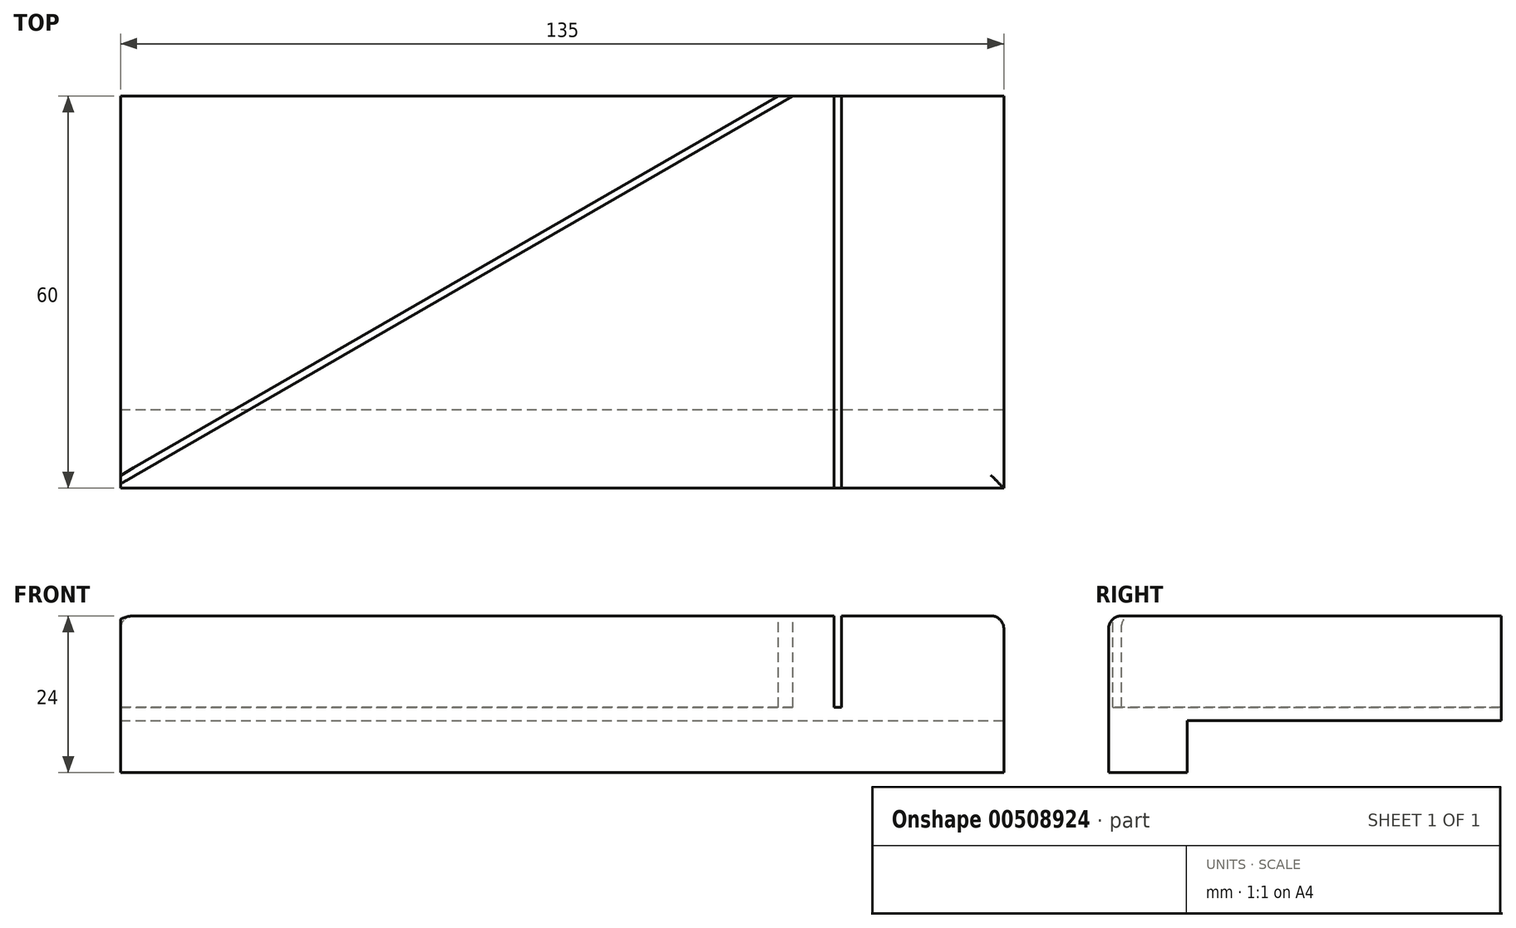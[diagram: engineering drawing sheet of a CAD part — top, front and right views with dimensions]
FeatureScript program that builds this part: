
annotation { "Feature Type Name" : "Feature", "Feature Type Description" : "" }
export const myFeature = defineFeature(function(context is Context, id is Id, definition is map)
    precondition{}
    {
        {
            var Q0;
            Q0=qCreatedBy(makeId("Top.planeOp"),FACE);
            var sketch = newSketch(context, id + "F0", { "sketchPlane" : qUnion([Q0])});
            skLineSegment(sketch, "E0.bottom", {"start": v(67.5, -30) * mm, "end": v(-67.5, -30) * mm});
            skLineSegment(sketch, "E0.top", {"start": v(67.5, 30) * mm, "end": v(-67.5, 30) * mm});
            skLineSegment(sketch, "E0.left", {"start": v(67.5, -30) * mm, "end": v(67.5, 30) * mm});
            skLineSegment(sketch, "E0.right", {"start": v(-67.5, -30) * mm, "end": v(-67.5, 30) * mm});
            skPoint(sketch, "E0.middle", {"position": v(0, 0) * mm});
            skSolve(sketch);
        }
        {
            var Q0;
            Q0 = qSketchRegion(id + "F0", true);
            extrude(context, id + "F1", {"entities" : qUnion([Q0]), "depth" : 16 * mm});
        }
        {
            var Q0;
            Q0=makeQuery(id+"F1.opExtrude","CAP_FACE",FACE,{"disambiguationData":[OSD([sQuery(id+"F0.wireOp",EDGE,"E0.bottom"),sQuery(id+"F0.wireOp",EDGE,"E0.top"),sQuery(id+"F0.wireOp",EDGE,"E0.left"),sQuery(id+"F0.wireOp",EDGE,"E0.right")])],"isStart":false});
            var sketch = newSketch(context, id + "F2", { "sketchPlane" : qUnion([Q0])});
            skLineSegment(sketch, "E1", {"start": v(15.2, 30) * mm, "end": v(-67.5, -17.74) * mm});
            skLineSegment(sketch, "E2", {"start": v(33.03, 30) * mm, "end": v(-67.5, -28.04) * mm});
            skLineSegment(sketch, "E3", {"start": v(41.55, 30) * mm, "end": v(41.55, -30) * mm});
            skLineSegment(sketch, "E4", {"start": v(-67.5, -18.78) * mm, "end": v(17, 30) * mm});
            skLineSegment(sketch, "E5", {"start": v(-67.5, -29.33) * mm, "end": v(35.27, 30) * mm});
            skLineSegment(sketch, "E6", {"start": v(15.2, 30) * mm, "end": v(17, 30) * mm});
            skLineSegment(sketch, "E7", {"start": v(33.03, 30) * mm, "end": v(35.27, 30) * mm});
            skLineSegment(sketch, "E8", {"start": v(-67.5, -29.33) * mm, "end": v(-67.5, -28.04) * mm});
            skLineSegment(sketch, "E9", {"start": v(-67.5, -18.78) * mm, "end": v(-67.5, -17.74) * mm});
            skLineSegment(sketch, "E10", {"start": v(41.55, 30) * mm, "end": v(42.67, 30) * mm});
            skLineSegment(sketch, "E11", {"start": v(42.67, 30) * mm, "end": v(42.67, -30) * mm});
            skLineSegment(sketch, "E12", {"start": v(42.67, -30) * mm, "end": v(41.55, -30) * mm});
            skLineSegment(sketch, "E13", {"start": v(-67.5, -29.33) * mm, "end": v(27.72, -29.33) * mm, "construction": true});
            skLineSegment(sketch, "E14", {"start": v(-67.5, -28.04) * mm, "end": v(-66.94, -29) * mm, "construction": true});
            skLineSegment(sketch, "E15", {"start": v(-67.5, -17.74) * mm, "end": v(-67.05, -18.52) * mm, "construction": true});
            skSolve(sketch);
        }
        {
            var Q0;
            Q0=makeQuery(id+"F2.imprint","IMPRINT",FACE,{"disambiguationData":[TD([[makeQuery(id+"F2.imprint","IMPRINT",EDGE,{"derivedFrom":sQuery(id+"F2.wireOp",EDGE,"E1")}),1.0]])]});
            var Q1;
            Q1=makeQuery(id+"F2.imprint","IMPRINT",FACE,{"disambiguationData":[TD([[makeQuery(id+"F2.imprint","IMPRINT",EDGE,{"derivedFrom":sQuery(id+"F2.wireOp",EDGE,"E2")}),1.0]])]});
            var Q2;
            Q2=makeQuery(id+"F2.imprint","IMPRINT",FACE,{"disambiguationData":[TD([[makeQuery(id+"F2.imprint","IMPRINT",EDGE,{"derivedFrom":sQuery(id+"F2.wireOp",EDGE,"E3")}),1.0]])]});
            extrude(context, id + "F3", {"entities" : qUnion([Q0, Q1, Q2]), "operationType" : NewBodyOperationType.REMOVE, "oppositeDirection" : true, "depth" : 14 * mm});
        }
        {
            var Q0;
            {var subQ0=sQuery(id+"F0.wireOp",EDGE,"E0.bottom");var subQ1=sQuery(id+"F0.wireOp",EDGE,"E0.right");Q0=makeQuery(id+"F3.boolean.opBoolean","SPLIT",EDGE,{"disambiguationData":[TD([makeQuery(id+"F1.opExtrude","SWEPT_FACE",FACE,{"disambiguationData":[OSD([subQ1])]})])],"derivedFrom":makeQuery(id+"F1.opExtrude","CAP_EDGE",EDGE,{"disambiguationData":[OSD([subQ0])],"isStart":false})});}
            var Q1;
            {var subQ0=sQuery(id+"F0.wireOp",EDGE,"E0.right");var subQ1=sQuery(id+"F0.wireOp",EDGE,"E0.top");Q1=makeQuery(id+"F3.boolean.opBoolean","SPLIT",EDGE,{"disambiguationData":[TD([makeQuery(id+"F1.opExtrude","SWEPT_FACE",FACE,{"disambiguationData":[OSD([subQ1])]})])],"derivedFrom":makeQuery(id+"F1.opExtrude","CAP_EDGE",EDGE,{"disambiguationData":[OSD([subQ0])],"isStart":false})});}
            var Q2;
            Q2=makeQuery(id+"F1.opExtrude","CAP_EDGE",EDGE,{"disambiguationData":[OSD([sQuery(id+"F0.wireOp",EDGE,"E0.left")])],"isStart":false});
            var Q3;
            {var subQ0=sQuery(id+"F0.wireOp",EDGE,"E0.bottom");var subQ1=sQuery(id+"F0.wireOp",EDGE,"E0.left");Q3=makeQuery(id+"F3.boolean.opBoolean","SPLIT",EDGE,{"disambiguationData":[TD([makeQuery(id+"F1.opExtrude","SWEPT_FACE",FACE,{"disambiguationData":[OSD([subQ1])]})])],"derivedFrom":makeQuery(id+"F1.opExtrude","CAP_EDGE",EDGE,{"disambiguationData":[OSD([subQ0])],"isStart":false})});}
            fillet(context, id + "F4", {"entities" : qUnion([Q0, Q1, Q2, Q3]), "radius" : 2 * mm, "tangentPropagation" : true, "allowEdgeOverflow" : false});
        }
        {
            var Q0;
            Q0=makeQuery(id+"F1.opExtrude","CAP_FACE",FACE,{"disambiguationData":[OSD([sQuery(id+"F0.wireOp",EDGE,"E0.bottom"),sQuery(id+"F0.wireOp",EDGE,"E0.top"),sQuery(id+"F0.wireOp",EDGE,"E0.left"),sQuery(id+"F0.wireOp",EDGE,"E0.right")])],"isStart":true});
            var sketch = newSketch(context, id + "F5", { "sketchPlane" : qUnion([Q0])});
            skLineSegment(sketch, "E16", {"start": v(0, 18) * mm, "end": v(0, -30) * mm, "construction": true});
            skLineSegment(sketch, "E17", {"start": v(-67.5, 18) * mm, "end": v(67.5, 18) * mm});
            skLineSegment(sketch, "E18", {"start": v(67.5, 18) * mm, "end": v(67.5, 30) * mm});
            skLineSegment(sketch, "E19", {"start": v(67.5, 30) * mm, "end": v(-67.5, 30) * mm});
            skLineSegment(sketch, "E20", {"start": v(-67.5, 30) * mm, "end": v(-67.5, 18) * mm});
            skSolve(sketch);
        }
        {
            var Q0;
            Q0 = qSketchRegion(id + "F5", true);
            extrude(context, id + "F6", {"entities" : qUnion([Q0]), "operationType" : NewBodyOperationType.ADD, "depth" : 8 * mm});
        }
    });
